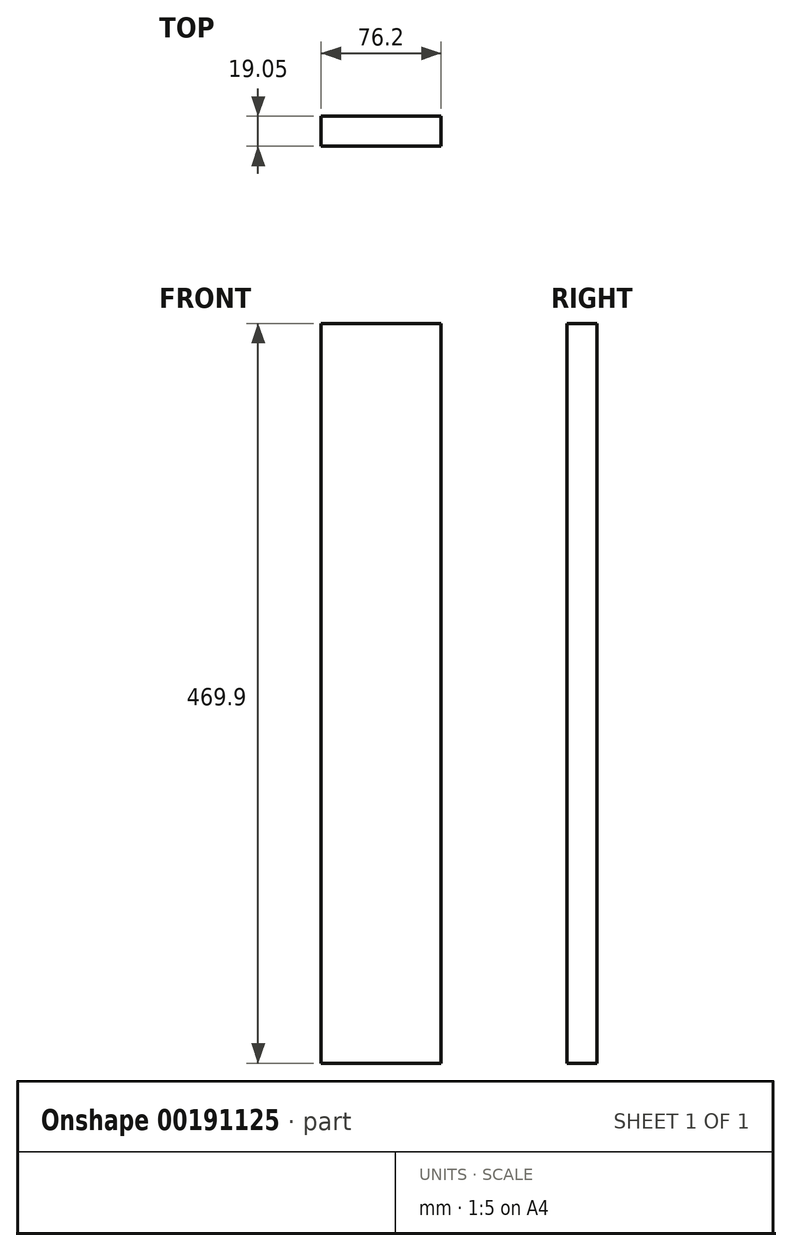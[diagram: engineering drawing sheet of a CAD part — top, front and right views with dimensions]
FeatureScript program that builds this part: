
annotation { "Feature Type Name" : "Feature", "Feature Type Description" : "" }
export const myFeature = defineFeature(function(context is Context, id is Id, definition is map)
    precondition{}
    {
        {
            var Q0;
            Q0=qCreatedBy(makeId("Front.planeOp"),FACE);
            var sketch = newSketch(context, id + "F0", { "sketchPlane" : qUnion([Q0])});
            skLineSegment(sketch, "E0.bottom", {"start": v(38.1, 234.95) * mm, "end": v(-38.1, 234.95) * mm});
            skLineSegment(sketch, "E0.top", {"start": v(38.1, -234.95) * mm, "end": v(-38.1, -234.95) * mm});
            skLineSegment(sketch, "E0.left", {"start": v(38.1, 234.95) * mm, "end": v(38.1, -234.95) * mm});
            skLineSegment(sketch, "E0.right", {"start": v(-38.1, 234.95) * mm, "end": v(-38.1, -234.95) * mm});
            skPoint(sketch, "E0.middle", {"position": v(0, 0) * mm});
            skSolve(sketch);
        }
        {
            var Q0;
            Q0 = qSketchRegion(id + "F0", true);
            extrude(context, id + "F1", {"entities" : qUnion([Q0]), "depth" : 19.05 * mm});
        }
    });
